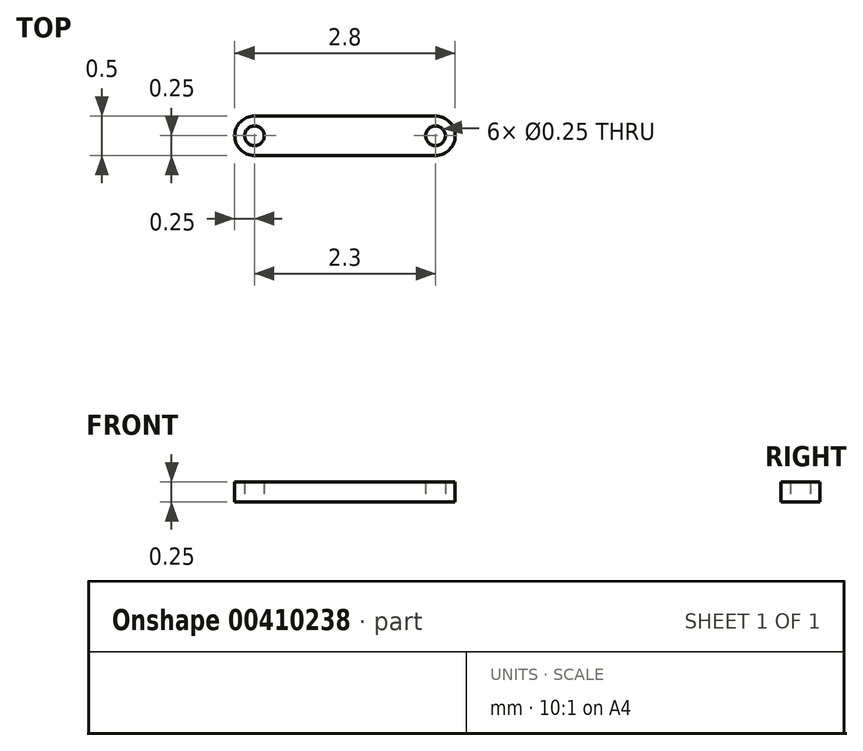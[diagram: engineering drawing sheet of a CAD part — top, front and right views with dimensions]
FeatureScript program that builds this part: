
annotation { "Feature Type Name" : "Feature", "Feature Type Description" : "" }
export const myFeature = defineFeature(function(context is Context, id is Id, definition is map)
    precondition{}
    {
        {
            var Q0;
            Q0=qCreatedBy(makeId("Top.planeOp"),FACE);
            var sketch = newSketch(context, id + "F0", { "sketchPlane" : qUnion([Q0])});
            skLineSegment(sketch, "E0.bottom", {"start": v(0, 0) * mm, "end": v(2.3, 0) * mm});
            skLineSegment(sketch, "E0.top", {"start": v(0, 0.5) * mm, "end": v(2.3, 0.5) * mm});
            skArc(sketch, "E1", {"start": v(2.3, 0) * mm, "mid": v(2.55, 0.25) * mm, "end": v(2.3, 0.5) * mm});
            skArc(sketch, "E2", {"start": v(0, 0.5) * mm, "mid": v(-0.25, 0.25) * mm, "end": v(0, 0) * mm});
            skCircle(sketch, "E3", {"center": v(0, 0.25) * mm, "radius": 0.12 * mm});
            skCircle(sketch, "E4", {"center": v(2.3, 0.25) * mm, "radius": 0.12 * mm});
            skSolve(sketch);
        }
        {
            var Q0;
            Q0=makeQuery(id+"F0.imprint","IMPRINT",FACE,{"disambiguationData":[TD([[makeQuery(id+"F0.imprint","IMPRINT",EDGE,{"derivedFrom":sQuery(id+"F0.wireOp",EDGE,"E0.bottom")}),1.0]])]});
            extrude(context, id + "F1", {"entities" : qUnion([Q0]), "depth" : 0.25 * mm});
        }
    });
